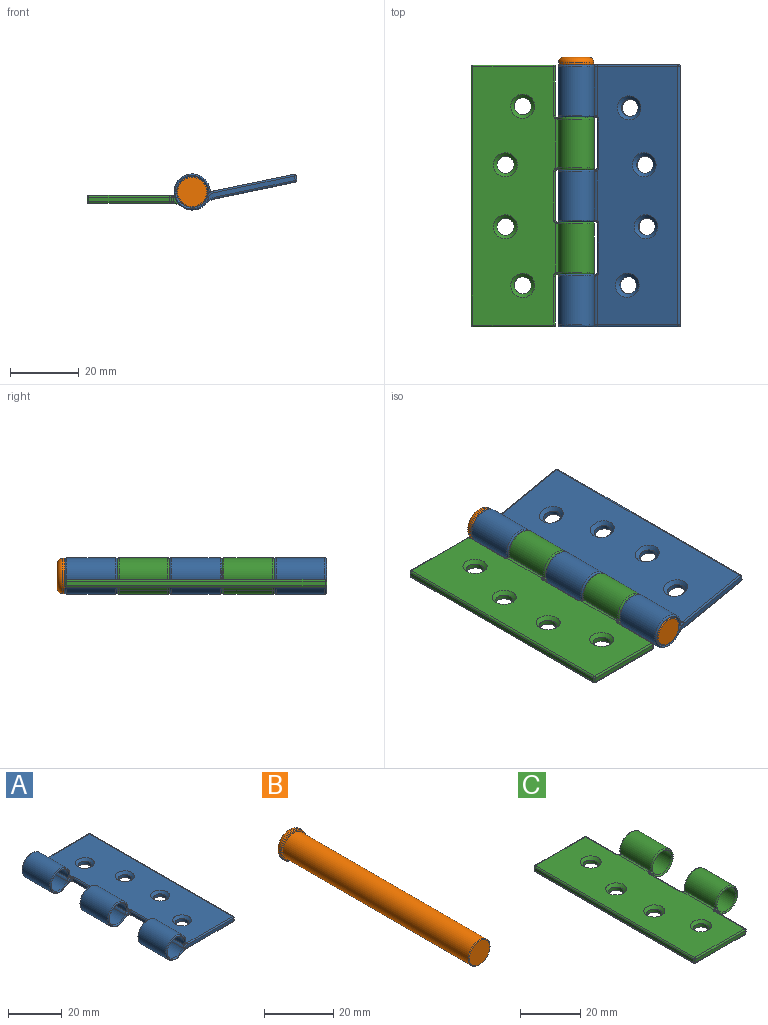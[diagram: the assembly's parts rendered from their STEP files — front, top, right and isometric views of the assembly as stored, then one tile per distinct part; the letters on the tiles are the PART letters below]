
ASSEMBLY  parts=3 mates=2
PART A: 94 faces, bbox 36.3x76x11.6 mm
  f0: cylinder r=5.25mm len=14.2mm, axis (0,1,0), area 412.4mm2, adj f2,f8,f61,f79
  f1: cylinder r=5.25mm len=14.2mm, axis (0,1,0), area 412.4mm2, adj f3,f9,f38,f70
  f2: plane 15.21x0.8mm, normal (0,0,-1), area 11.4mm2, adj f0,f4,f61,f63,f79,f82
  f3: plane 15.21x0.8mm, normal (0,0,-1), area 11.4mm2, adj f1,f5,f37,f38,f70,f72
  f4: cylinder r=4.5mm len=14.2mm, axis (0,1,0), area 382.9mm2, adj f2,f6,f63,f82
  f5: cylinder r=4.5mm len=14.2mm, axis (0,1,0), area 382.9mm2, adj f3,f7,f37,f72
  f6: cylinder r=2.39mm len=14.47mm, axis (0,1,0), area 36mm2, adj f4,f14,f65,f67,f84,f85
  f7: cylinder r=2.39mm len=14.33mm, axis (0,1,0), area 35.9mm2, adj f5,f14,f35,f74,f76
  f8: cylinder r=4.96mm len=14.47mm, axis (0,1,0), area 44.3mm2, adj f0,f16,f58,f60,f77,f80
  f9: cylinder r=4.96mm len=14.33mm, axis (0,1,0), area 44.3mm2, adj f1,f16,f40,f68,f69
  f10: cylinder r=5.25mm len=14.2mm, axis (0,1,0), area 412.4mm2, adj f11,f17,f43,f52
  f11: plane 15.21x0.8mm, normal (0,0,-1), area 11.4mm2, adj f10,f12,f43,f44,f52,f55
  f12: cylinder r=4.5mm len=14.2mm, axis (0,1,0), area 382.9mm2, adj f11,f13,f44,f55
  f13: cylinder r=2.39mm len=14.33mm, axis (0,1,0), area 35.9mm2, adj f12,f14,f41,f57,f59
  f14: plane 75x24mm, normal (0,0,1), area 1630.6mm2, adj f6,f7,f13,f33,f34,f39,f62,f64
  f15: plane 75x1.3mm, normal (1,0,0), area 97.5mm2, adj f30,f31,f34,f47
  f16: plane 75x24mm, normal (0,0,-1), area 1706mm2, adj f8,f9,f17,f42,f47,f48,f51,f54
  f17: cylinder r=4.96mm len=14.33mm, axis (0,1,0), area 44.3mm2, adj f10,f16,f46,f50,f53
  f18: plane 26.22x1.77mm, normal (0,-1,0), area 33.2mm2, adj f31,f39,f41,f44,f46,f48
  f19: plane 26.22x1.77mm, normal (0,1,0), area 33.2mm2, adj f30,f33,f35,f37,f40,f42
  f20: plane 14.2x1.3mm, normal (-1,0,0), area 18.5mm2, adj f26,f27,f73,f81
  f21: plane 1.72x1.7mm, normal (0,-1,0), area 1.3mm2, adj f26,f69,f72,f74
  f22: plane 1.72x1.7mm, normal (0,1,0), area 1.3mm2, adj f27,f80,f82,f84
  f23: plane 14.2x1.3mm, normal (-1,0,0), area 18.5mm2, adj f28,f29,f54,f64
  f24: plane 1.72x1.7mm, normal (0,1,0), area 1.3mm2, adj f28,f53,f55,f57
  f25: plane 1.72x1.7mm, normal (0,-1,0), area 1.3mm2, adj f29,f60,f63,f65
  f26: cylinder r=0.5mm len=1.32mm, axis (0,0,-1), area 1mm2, adj f20,f21,f68,f71,f76,f78
  f27: cylinder r=0.5mm len=1.32mm, axis (0,0,1), area 1mm2, adj f20,f22,f75,f77,f83,f85
  f28: cylinder r=0.5mm len=1.32mm, axis (0,0,-1), area 1mm2, adj f23,f24,f50,f51,f59,f62
  f29: cylinder r=0.5mm len=1.32mm, axis (0,0,1), area 1mm2, adj f23,f25,f56,f58,f66,f67
  f30: cylinder r=0.5mm len=1.3mm, axis (0,0,-1), area 1mm2, adj f15,f19,f32,f45
  f31: cylinder r=0.5mm len=1.3mm, axis (0,0,1), area 1mm2, adj f15,f18,f36,f49
  f32: sphere r=0.5mm, area 0.4mm2, adj f30,f33,f34
  f33: cylinder r=0.5mm len=24mm, axis (1,0,0), area 18.8mm2, adj f14,f19,f32,f35
  f34: cylinder r=0.5mm len=75mm, axis (0,1,0), area 58.9mm2, adj f14,f15,f32,f36
  f35: torus R=1.89mm, axis (0,-1,0), area 1.8mm2, adj f7,f19,f33,f37
  f36: sphere r=0.5mm, area 0.4mm2, adj f31,f34,f39
  f37: torus R=5mm, axis (0,-1,0), area 18.5mm2, adj f3,f5,f19,f35,f38,f40
  f38: torus R=4.75mm, axis (0,-1,0), area 18.7mm2, adj f1,f3,f37,f40
  f39: cylinder r=0.5mm len=24mm, axis (-1,0,0), area 18.8mm2, adj f14,f18,f36,f41
  f40: torus R=5.46mm, axis (0,-1,0), area 2.5mm2, adj f9,f19,f37,f38,f42
  f41: torus R=1.89mm, axis (0,-1,0), area 1.8mm2, adj f13,f18,f39,f44
  f42: cylinder r=0.5mm len=24mm, axis (-1,0,0), area 18.8mm2, adj f16,f19,f40,f45
  f43: torus R=4.75mm, axis (0,-1,0), area 18.7mm2, adj f10,f11,f44,f46
  f44: torus R=5mm, axis (0,-1,0), area 18.5mm2, adj f11,f12,f18,f41,f43,f46
  f45: sphere r=0.5mm, area 0.4mm2, adj f30,f42,f47
  f46: torus R=5.46mm, axis (0,-1,0), area 2.5mm2, adj f17,f18,f43,f44,f48
  f47: cylinder r=0.5mm len=75mm, axis (0,1,0), area 58.9mm2, adj f15,f16,f45,f49
  f48: cylinder r=0.5mm len=24mm, axis (1,0,0), area 18.8mm2, adj f16,f18,f46,f49
  f49: sphere r=0.5mm, area 0.4mm2, adj f31,f47,f48
  f50: bspline ~0.72x0.61mm, area 0.3mm2, adj f17,f28,f51,f53
  f51: torus R=1mm, axis (0,0,1), area 0.6mm2, adj f16,f28,f50,f54
  f52: torus R=4.75mm, axis (0,-1,0), area 18.7mm2, adj f10,f11,f53,f55
  f53: torus R=5.46mm, axis (0,-1,0), area 2.1mm2, adj f17,f24,f50,f52,f55
  f54: cylinder r=0.5mm len=14.2mm, axis (0,-1,0), area 11.2mm2, adj f16,f23,f51,f56
  f55: torus R=5mm, axis (0,-1,0), area 18.5mm2, adj f11,f12,f24,f52,f53,f57
  f56: torus R=1mm, axis (0,0,1), area 0.6mm2, adj f16,f29,f54,f58
  f57: torus R=1.89mm, axis (0,-1,0), area 1.4mm2, adj f13,f24,f55,f59
  f58: bspline ~0.72x0.61mm, area 0.3mm2, adj f8,f29,f56,f60
  f59: bspline ~0.83x0.6mm, area 0.3mm2, adj f13,f28,f57,f62
  f60: torus R=5.46mm, axis (0,-1,0), area 2.1mm2, adj f8,f25,f58,f61,f63
  f61: torus R=4.75mm, axis (0,-1,0), area 18.7mm2, adj f0,f2,f60,f63
  f62: torus R=1mm, axis (0,0,-1), area 0.6mm2, adj f14,f28,f59,f64
  f63: torus R=5mm, axis (0,-1,0), area 18.5mm2, adj f2,f4,f25,f60,f61,f65
  f64: cylinder r=0.5mm len=14.2mm, axis (0,-1,0), area 11.2mm2, adj f14,f23,f62,f66
  f65: torus R=1.89mm, axis (0,-1,0), area 1.4mm2, adj f6,f25,f63,f67
  f66: torus R=1mm, axis (0,0,-1), area 0.6mm2, adj f14,f29,f64,f67
  f67: bspline ~0.83x0.6mm, area 0.3mm2, adj f6,f29,f65,f66
  f68: bspline ~0.72x0.61mm, area 0.3mm2, adj f9,f26,f69,f71
  f69: torus R=5.46mm, axis (0,-1,0), area 2.1mm2, adj f9,f21,f68,f70,f72
  f70: torus R=4.75mm, axis (0,-1,0), area 18.7mm2, adj f1,f3,f69,f72
  f71: torus R=1mm, axis (0,0,1), area 0.6mm2, adj f16,f26,f68,f73
  f72: torus R=5mm, axis (0,-1,0), area 18.5mm2, adj f3,f5,f21,f69,f70,f74
  f73: cylinder r=0.5mm len=14.2mm, axis (0,1,0), area 11.2mm2, adj f16,f20,f71,f75
  f74: torus R=1.89mm, axis (0,-1,0), area 1.4mm2, adj f7,f21,f72,f76
  f75: torus R=1mm, axis (0,0,1), area 0.6mm2, adj f16,f27,f73,f77
  f76: bspline ~0.83x0.6mm, area 0.3mm2, adj f7,f26,f74,f78
  f77: bspline ~0.72x0.61mm, area 0.3mm2, adj f8,f27,f75,f80
  f78: torus R=1mm, axis (0,0,-1), area 0.6mm2, adj f14,f26,f76,f81
  f79: torus R=4.75mm, axis (0,-1,0), area 18.7mm2, adj f0,f2,f80,f82
  f80: torus R=5.46mm, axis (0,-1,0), area 2.1mm2, adj f8,f22,f77,f79,f82
  f81: cylinder r=0.5mm len=14.2mm, axis (0,-1,0), area 11.2mm2, adj f14,f20,f78,f83
  f82: torus R=5mm, axis (0,-1,0), area 18.5mm2, adj f2,f4,f22,f79,f80,f84
  f83: torus R=1mm, axis (0,0,-1), area 0.6mm2, adj f14,f27,f81,f85
  f84: torus R=1.89mm, axis (0,-1,0), area 1.4mm2, adj f6,f22,f82,f85
  f85: bspline ~0.83x0.6mm, area 0.3mm2, adj f6,f27,f83,f84
  f86: cylinder r=2.5mm len=5mm, axis (0,0,1), area 20.4mm2, adj f16,f91
  f87: cylinder r=2.5mm len=5mm, axis (0,0,1), area 20.4mm2, adj f16,f90
  f88: cylinder r=2.5mm len=5mm, axis (0,0,1), area 20.4mm2, adj f16,f92
  f89: cylinder r=2.5mm len=5mm, axis (0,0,1), area 20.4mm2, adj f16,f93
  f90: cone r=2.5mm half-angle=45deg, axis (0,0,1), area 26.7mm2, adj f14,f87
  f91: cone r=2.5mm half-angle=45deg, axis (0,0,1), area 26.7mm2, adj f14,f86
  f92: cone r=2.5mm half-angle=45deg, axis (0,0,1), area 26.7mm2, adj f14,f88
  f93: cone r=2.5mm half-angle=45deg, axis (0,0,1), area 26.7mm2, adj f14,f89
PART B: 8 faces, bbox 11x78.2x11 mm
  f0: cylinder r=4.4mm len=75.8mm, axis (0,1,0), area 2095.6mm2, adj f2,f5
  f1: plane 8.4x8.4mm, normal (0,-1,0), area 55.4mm2, adj f2
  f2: torus R=4.2mm, axis (0,-1,0), area 8.5mm2, adj f0,f1
  f3: cylinder r=5.1mm len=10.21mm, axis (0,-1,0), area 16mm2, adj f6,f7
  f4: plane 7.21x7.21mm, normal (0,1,0), area 40.8mm2, adj f6
  f5: plane 9.81x9.81mm, normal (0,-1,0), area 14.7mm2, adj f0,f7
  f6: torus R=3.6mm, axis (0,1,0), area 67.5mm2, adj f3,f4
  f7: torus R=4.9mm, axis (0,1,0), area 9.9mm2, adj f3,f5
PART C: 90 faces, bbox 36.3x76x11.6 mm
  f0: plane 75x24mm, normal (0,0,1), area 1623.5mm2, adj f8,f9,f47,f49,f54,f58,f59,f61
  f1: plane 75x24mm, normal (0,0,-1), area 1698.9mm2, adj f10,f11,f31,f32,f34,f35,f40,f44
  f2: cylinder r=5.25mm len=14.2mm, axis (0,1,0), area 412.4mm2, adj f4,f10,f51,f75
  f3: cylinder r=5.25mm len=14.2mm, axis (0,1,0), area 412.4mm2, adj f5,f11,f38,f66
  f4: plane 15.21x0.8mm, normal (0,0,-1), area 11.4mm2, adj f2,f6,f51,f53,f75,f78
  f5: plane 15.21x0.8mm, normal (0,0,-1), area 11.4mm2, adj f3,f7,f38,f41,f66,f68
  f6: cylinder r=4.5mm len=14.2mm, axis (0,1,0), area 382.9mm2, adj f4,f8,f53,f78
  f7: cylinder r=4.5mm len=14.2mm, axis (0,1,0), area 382.9mm2, adj f5,f9,f41,f68
  f8: cylinder r=2.39mm len=14.47mm, axis (0,1,0), area 36mm2, adj f0,f6,f55,f57,f80,f81
  f9: cylinder r=2.39mm len=14.47mm, axis (0,1,0), area 36mm2, adj f0,f7,f43,f45,f70,f72
  f10: cylinder r=4.96mm len=14.47mm, axis (0,1,0), area 44.3mm2, adj f1,f2,f48,f50,f73,f76
  f11: cylinder r=4.96mm len=14.47mm, axis (0,1,0), area 44.3mm2, adj f1,f3,f36,f39,f64,f65
  f12: plane 75x1.3mm, normal (-1,0,0), area 97.5mm2, adj f28,f29,f35,f58
  f13: plane 23.5x1.3mm, normal (0,-1,0), area 30.6mm2, adj f22,f29,f31,f54
  f14: plane 23.5x1.3mm, normal (0,1,0), area 30.6mm2, adj f26,f28,f40,f62
  f15: plane 14.2x1.3mm, normal (1,0,0), area 18.5mm2, adj f22,f23,f32,f49
  f16: plane 1.72x1.7mm, normal (0,-1,0), area 1.3mm2, adj f23,f39,f41,f43
  f17: plane 14.2x1.3mm, normal (1,0,0), area 18.5mm2, adj f24,f25,f69,f77
  f18: plane 1.72x1.7mm, normal (0,1,0), area 1.3mm2, adj f24,f65,f68,f70
  f19: plane 1.72x1.7mm, normal (0,-1,0), area 1.3mm2, adj f25,f76,f78,f80
  f20: plane 14.2x1.3mm, normal (1,0,0), area 18.5mm2, adj f26,f27,f44,f61
  f21: plane 1.72x1.7mm, normal (0,1,0), area 1.3mm2, adj f27,f50,f53,f55
  f22: cylinder r=0.5mm len=1.3mm, axis (0,0,1), area 1mm2, adj f13,f15,f30,f52
  f23: cylinder r=0.5mm len=1.32mm, axis (0,0,1), area 1mm2, adj f15,f16,f34,f36,f45,f47
  f24: cylinder r=0.5mm len=1.32mm, axis (0,0,-1), area 1mm2, adj f17,f18,f64,f67,f72,f74
  f25: cylinder r=0.5mm len=1.32mm, axis (0,0,1), area 1mm2, adj f17,f19,f71,f73,f79,f81
  f26: cylinder r=0.5mm len=1.3mm, axis (0,0,-1), area 1mm2, adj f14,f20,f42,f63
  f27: cylinder r=0.5mm len=1.32mm, axis (0,0,-1), area 1mm2, adj f20,f21,f46,f48,f57,f59
  f28: cylinder r=0.5mm len=1.3mm, axis (0,0,-1), area 1mm2, adj f12,f14,f37,f60
  f29: cylinder r=0.5mm len=1.3mm, axis (0,0,1), area 1mm2, adj f12,f13,f33,f56
  f30: sphere r=0.5mm, area 0.4mm2, adj f22,f31,f32
  f31: cylinder r=0.5mm len=23.5mm, axis (-1,0,0), area 18.5mm2, adj f1,f13,f30,f33
  f32: cylinder r=0.5mm len=14.2mm, axis (0,1,0), area 11.2mm2, adj f1,f15,f30,f34
  f33: sphere r=0.5mm, area 0.4mm2, adj f29,f31,f35
  f34: torus R=1mm, axis (0,0,1), area 0.6mm2, adj f1,f23,f32,f36
  f35: cylinder r=0.5mm len=75mm, axis (0,1,0), area 58.9mm2, adj f1,f12,f33,f37
  f36: bspline ~0.72x0.61mm, area 0.3mm2, adj f11,f23,f34,f39
  f37: sphere r=0.5mm, area 0.4mm2, adj f28,f35,f40
  f38: torus R=4.75mm, axis (0,1,0), area 18.7mm2, adj f3,f5,f39,f41
  f39: torus R=5.46mm, axis (0,1,0), area 2.1mm2, adj f11,f16,f36,f38,f41
  f40: cylinder r=0.5mm len=23.5mm, axis (1,0,0), area 18.5mm2, adj f1,f14,f37,f42
  f41: torus R=5mm, axis (0,1,0), area 18.5mm2, adj f5,f7,f16,f38,f39,f43
  f42: sphere r=0.5mm, area 0.4mm2, adj f26,f40,f44
  f43: torus R=1.89mm, axis (0,1,0), area 1.4mm2, adj f9,f16,f41,f45
  f44: cylinder r=0.5mm len=14.2mm, axis (0,-1,0), area 11.2mm2, adj f1,f20,f42,f46
  f45: bspline ~0.83x0.6mm, area 0.3mm2, adj f9,f23,f43,f47
  f46: torus R=1mm, axis (0,0,1), area 0.6mm2, adj f1,f27,f44,f48
  f47: torus R=1mm, axis (0,0,-1), area 0.6mm2, adj f0,f23,f45,f49
  f48: bspline ~0.72x0.61mm, area 0.3mm2, adj f10,f27,f46,f50
  f49: cylinder r=0.5mm len=14.2mm, axis (0,1,0), area 11.2mm2, adj f0,f15,f47,f52
  f50: torus R=5.46mm, axis (0,1,0), area 2.1mm2, adj f10,f21,f48,f51,f53
  f51: torus R=4.75mm, axis (0,1,0), area 18.7mm2, adj f2,f4,f50,f53
  f52: sphere r=0.5mm, area 0.4mm2, adj f22,f49,f54
  f53: torus R=5mm, axis (0,1,0), area 18.5mm2, adj f4,f6,f21,f50,f51,f55
  f54: cylinder r=0.5mm len=23.5mm, axis (1,0,0), area 18.5mm2, adj f0,f13,f52,f56
  f55: torus R=1.89mm, axis (0,1,0), area 1.4mm2, adj f8,f21,f53,f57
  f56: sphere r=0.5mm, area 0.4mm2, adj f29,f54,f58
  f57: bspline ~0.83x0.6mm, area 0.3mm2, adj f8,f27,f55,f59
  f58: cylinder r=0.5mm len=75mm, axis (0,1,0), area 58.9mm2, adj f0,f12,f56,f60
  f59: torus R=1mm, axis (0,0,-1), area 0.6mm2, adj f0,f27,f57,f61
  f60: sphere r=0.5mm, area 0.4mm2, adj f28,f58,f62
  f61: cylinder r=0.5mm len=14.2mm, axis (0,1,0), area 11.2mm2, adj f0,f20,f59,f63
  f62: cylinder r=0.5mm len=23.5mm, axis (-1,0,0), area 18.5mm2, adj f0,f14,f60,f63
  f63: sphere r=0.5mm, area 0.4mm2, adj f26,f61,f62
  f64: bspline ~0.72x0.61mm, area 0.3mm2, adj f11,f24,f65,f67
  f65: torus R=5.46mm, axis (0,1,0), area 2.1mm2, adj f11,f18,f64,f66,f68
  f66: torus R=4.75mm, axis (0,1,0), area 18.7mm2, adj f3,f5,f65,f68
  f67: torus R=1mm, axis (0,0,1), area 0.6mm2, adj f1,f24,f64,f69
  f68: torus R=5mm, axis (0,1,0), area 18.5mm2, adj f5,f7,f18,f65,f66,f70
  f69: cylinder r=0.5mm len=14.2mm, axis (0,1,0), area 11.2mm2, adj f1,f17,f67,f71
  f70: torus R=1.89mm, axis (0,1,0), area 1.4mm2, adj f9,f18,f68,f72
  f71: torus R=1mm, axis (0,0,1), area 0.6mm2, adj f1,f25,f69,f73
  f72: bspline ~0.83x0.6mm, area 0.3mm2, adj f9,f24,f70,f74
  f73: bspline ~0.72x0.61mm, area 0.3mm2, adj f10,f25,f71,f76
  f74: torus R=1mm, axis (0,0,-1), area 0.6mm2, adj f0,f24,f72,f77
  f75: torus R=4.75mm, axis (0,1,0), area 18.7mm2, adj f2,f4,f76,f78
  f76: torus R=5.46mm, axis (0,1,0), area 2.1mm2, adj f10,f19,f73,f75,f78
  f77: cylinder r=0.5mm len=14.2mm, axis (0,1,0), area 11.2mm2, adj f0,f17,f74,f79
  f78: torus R=5mm, axis (0,1,0), area 18.5mm2, adj f4,f6,f19,f75,f76,f80
  f79: torus R=1mm, axis (0,0,-1), area 0.6mm2, adj f0,f25,f77,f81
  f80: torus R=1.89mm, axis (0,1,0), area 1.4mm2, adj f8,f19,f78,f81
  f81: bspline ~0.83x0.6mm, area 0.3mm2, adj f8,f25,f79,f80
  f82: cylinder r=2.5mm len=5mm, axis (0,0,1), area 20.4mm2, adj f1,f87
  f83: cylinder r=2.5mm len=5mm, axis (0,0,1), area 20.4mm2, adj f1,f86
  f84: cylinder r=2.5mm len=5mm, axis (0,0,1), area 20.4mm2, adj f1,f88
  f85: cylinder r=2.5mm len=5mm, axis (0,0,1), area 20.4mm2, adj f1,f89
  f86: cone r=3.5mm half-angle=45deg, axis (0,0,1), area 26.7mm2, adj f0,f83
  f87: cone r=2.5mm half-angle=45deg, axis (0,0,1), area 26.7mm2, adj f0,f82
  f88: cone r=3.5mm half-angle=45deg, axis (0,0,1), area 26.7mm2, adj f0,f84
  f89: cone r=2.5mm half-angle=45deg, axis (0,0,1), area 26.7mm2, adj f0,f85
PLACE A rot(axis=(0,-1,0),11.7deg) t=(7.96,-5.85,-3.34)mm
PLACE B t=(7.63,-5.83,-2.14)mm
PLACE C t=(7.63,-5.88,-2.14)mm fixed
MATE revolute C.f2 <-> A.f0  axis (0,1,0) through (13.63,-66.66,-1.14)mm
MATE revolute B.f0 <-> A.f0  axis (0,-1,0) through (13.63,-81.83,-1.14)mm
